# Revit family: RKSK 330_1800-xxx
name_source: partatom
category: Leuchten
units: mm (PartAtom-declared; Revit-internal decimal feet)

## family parameters
Basisbauteil = Fläche
Beim Laden mit Abzugskörper schneiden = Nein
Bemaßung runder Anschluss = Durchmesser verwenden
Gemeinsam genutzt = Nein
Lichtquelle = Ja
OmniClass-Nummer = 23.80.70.11
OmniClass-Titel = Luminaries for Internal Lighting
Raumberechnungspunkt = Nein
Teiletyp = Normal

## types (8) — shared parameters
Baugruppenkennzeichen = D5020200
Datei für fotometrisches Netz = RKSK 330xxx HPC.IES
Emissionsform beim Rendern sichtbar = Nein
Farbfilter = 16777215
Farbtemperaturverschiebung bei Dämpfen der Lampe = <Keine Auswahl>
Hersteller = RIDI Leuchten GmbH
Lampe = LED
Neigungswinkel = 90.00°
URL = www.ridi.de
Von Kreisdurchmesser aussenden = 360 mm  [stored 1.1811 ft]
brand = RIDI
conformity mark = CE
electrical safety class = 1
height = 144 mm  [stored 0.472441 ft]
ingress protection (IP) code = IP65
length = 360 mm  [stored 1.1811 ft]
nominal frequency = 50-60Hz
nominal voltage = 230
voltage type (AC, DC, UC) = AC
weight = 1,5 kg
width = 360 mm  [stored 1.1811 ft]
zero-valued in all types: Vorgabe-Ansicht

## per-type parameters (varying)
| type | Modell | Scheinlast | rated input power |
| RKSK 330_1800-830 HPC | 1420083 | 14 VA | 14 |
| RKSK 330_1800-830 HPC-DALI | 1430083 | 14 VA | 14 |
| RKSK 330_1800-840 HPC | 1420063 | 14 VA | 14 |
| RKSK 330_1800-840 HPC-DALI | 1430063 | 14 VA | 14 |
| RKSK 330_2500-830 HPC | 1420664 | 19 VA | 19 |
| RKSK 330_2500-830 HPC-DALI | 1430664 | 19 VA | 19 |
| RKSK 330_2500-840 HPC | 1420667 | 19 VA | 19 |
| RKSK 330_2500-840 HPC-DALI | 1430667 | 19 VA | 19 |

note: column(s) folded — value = type name in every type: product name

note: [stored X ft] marks values corroborated as IEEE doubles in the binary element streams (Revit-internal decimal feet)
